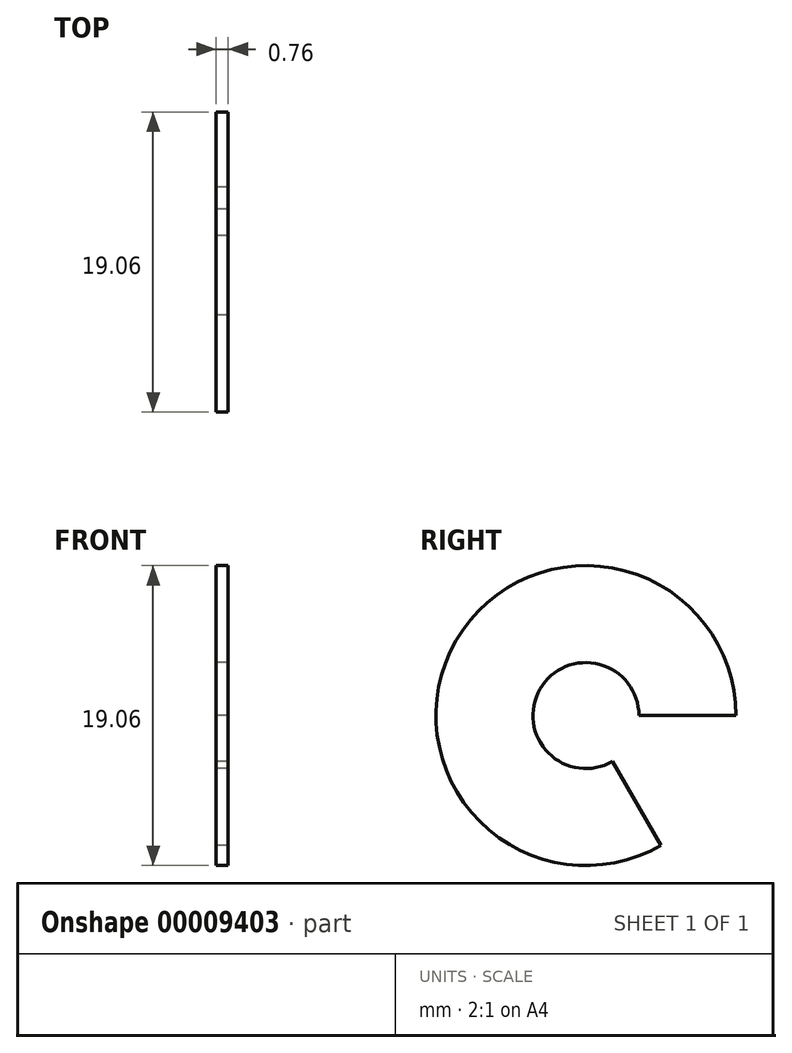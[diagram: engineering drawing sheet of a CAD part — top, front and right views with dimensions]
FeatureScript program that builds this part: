
annotation { "Feature Type Name" : "Feature", "Feature Type Description" : "" }
export const myFeature = defineFeature(function(context is Context, id is Id, definition is map)
    precondition{}
    {
        {
            var Q0;
            Q0=qCreatedBy(makeId("Top.planeOp"),FACE);
            var sketch = newSketch(context, id + "F0", { "sketchPlane" : qUnion([Q0])});
            skLineSegment(sketch, "E0.bottom", {"start": v(0, 3.37) * mm, "end": v(-0.76, 3.37) * mm});
            skLineSegment(sketch, "E0.top", {"start": v(0, 9.53) * mm, "end": v(-0.76, 9.53) * mm});
            skLineSegment(sketch, "E0.left", {"start": v(0, 3.37) * mm, "end": v(0, 9.53) * mm});
            skLineSegment(sketch, "E0.right", {"start": v(-0.76, 3.37) * mm, "end": v(-0.76, 9.53) * mm});
            skLineSegment(sketch, "E1", {"start": v(-9.37, 0) * mm, "end": v(9.37, 0) * mm});
            skSolve(sketch);
        }
        {
            var Q0;
            Q0=makeQuery(id+"F0.imprint","IMPRINT",FACE,{"disambiguationData":[TD([[makeQuery(id+"F0.imprint","IMPRINT",EDGE,{"derivedFrom":sQuery(id+"F0.wireOp",EDGE,"E0.bottom")}),-1.0]])]});
            var Q1;
            Q1=sQuery(id+"F0.wireOp",EDGE,"E1");
            revolve(context, id + "F1", {"surfaceOperationType" : NewSurfaceOperationType.NEW, "entities" : qUnion([Q0]), "axis" : qUnion([Q1]), "revolveType" : RevolveType.ONE_DIRECTION, "angle" : 300 * degree});
        }
    });
